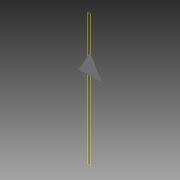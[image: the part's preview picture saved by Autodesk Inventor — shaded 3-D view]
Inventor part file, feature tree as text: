
AUTODESK INVENTOR PART (.ipt)
format: ipt  version: 2014 SP1 (Build 180222100, 222)  size: 100,864 bytes
history: native  units: in
note: dims shown in document units (in); Inventor stores cm internally (conversion verified against a paired STEP export)
features: reference x17, plane x1, extrude x1, fillet x1, sketch x1
ambient origin geometry x8: Origin, YZ Plane, XZ Plane, XY Plane, X Axis, Y Axis, Z Axis, Center Point
bodies: Solid1 (feature_tree)
feature tree (21):
  plane  "Work Plane1"
  extrude  "Extrusion1"  Depth=0.125in TaperAngle=0.0deg
  fillet  "Fillet1"  Radius=0.125in
  sketch  "Sketch1"  dims[d0=1.0in d1=0.125in d2=0.0in d3=0.125in]
  reference  "Reference1"
  reference  "Reference2"
  reference  "Reference3"
  reference  "Reference4"
  reference  "Reference5"
  reference  "Reference6"
  reference  "Reference7"
  reference  "Reference8"
  reference  "Reference9"
  reference  "Reference10"
  reference  "Reference11"
  reference  "Reference12"
  reference  "Reference13"
  reference  "Reference14"
  reference  "Reference15"
  reference  "Reference16"
  reference  "Reference17"
